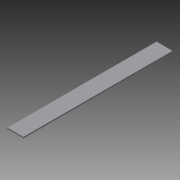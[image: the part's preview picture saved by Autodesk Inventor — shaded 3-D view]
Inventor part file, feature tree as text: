
AUTODESK INVENTOR PART (.ipt)
format: ipt  version: 2015 (Build 190159000, 159)  size: 67,584 bytes
history: native  units: in
note: dims shown in document units (in); Inventor stores cm internally (conversion verified against a paired STEP export)
features: extrude x1, sketch x1
ambient origin geometry x8: Origin, YZ Plane, XZ Plane, XY Plane, X Axis, Y Axis, Z Axis, Center Point
bodies: Solid1 (feature_tree)
feature tree (2):
  extrude  "Extrusion1"  Depth=0.125in
  sketch  "Sketch1"  dims[d0=1.5in d1=0.125in d2=14.0in d3=0.0in]
